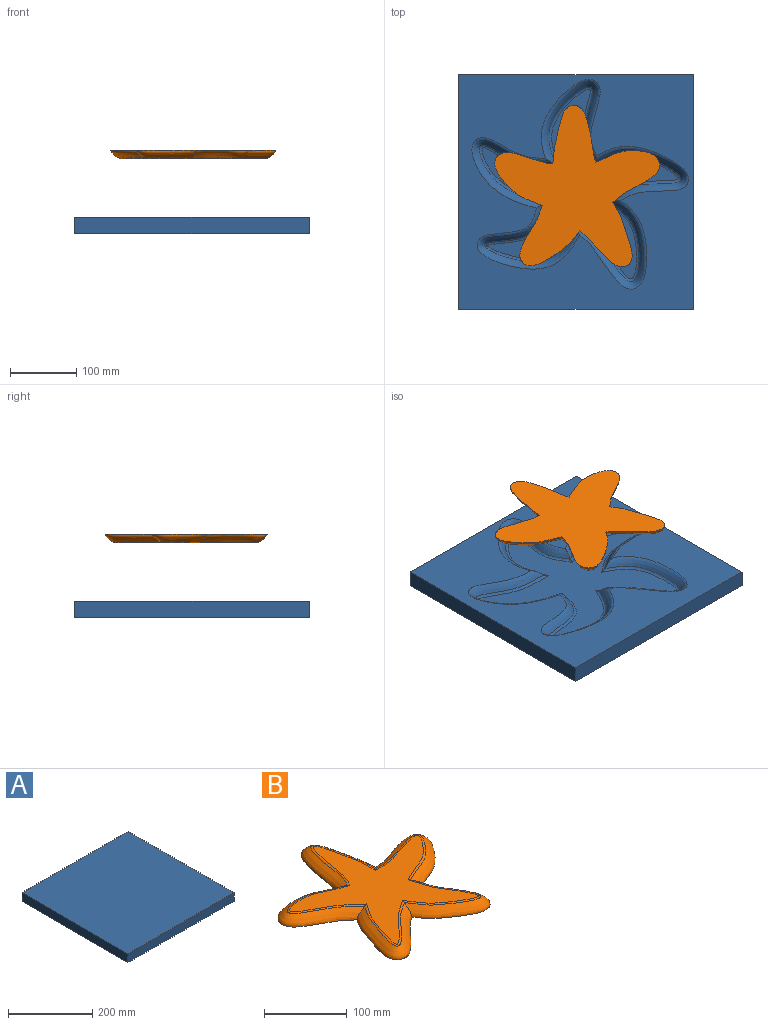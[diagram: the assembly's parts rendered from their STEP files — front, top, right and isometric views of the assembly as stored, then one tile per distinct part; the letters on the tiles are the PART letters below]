
ASSEMBLY  parts=2 mates=1
PART A: 19 faces, bbox 355.6x355.6x25.4 mm
  f0: plane 355.6x355.6mm, normal (0,0,-1), area 78097.3mm2, adj f1,f2,f3,f4,f7,f8,f9,f10
  f1: plane 355.6x25.4mm, normal (1,0,0), area 9032.2mm2, adj f0,f2,f4,f5
  f2: plane 355.6x25.4mm, normal (0,1,0), area 9032.2mm2, adj f0,f1,f3,f5
  f3: plane 355.6x25.4mm, normal (-1,0,0), area 9032.2mm2, adj f0,f2,f4,f5
  f4: plane 355.6x25.4mm, normal (0,-1,0), area 9032.2mm2, adj f0,f1,f3,f5
  f5: plane 355.6x355.6mm, normal (0,0,1), area 126451.4mm2, adj f1,f2,f3,f4
  f6: plane 297.23x287.11mm, normal (0,0,-1), area 27777.5mm2, adj f13,f14,f15,f16,f17,f18
  f7: bspline ~142.68x85.34mm, area 4168mm2, adj f0,f8,f11,f15,f17
  f8: bspline ~133.93x108.95mm, area 4339.6mm2, adj f0,f7,f9,f13,f15
  f9: bspline ~154.2x101.43mm, area 4797.9mm2, adj f0,f8,f10,f12,f13,f14,f16
  f10: bspline ~132.62x106.84mm, area 4198.7mm2, adj f0,f9,f11,f16,f18
  f11: bspline ~134.44x89.26mm, area 4397.8mm2, adj f0,f7,f10,f17,f18
  f12: bspline ~5.72x4.01mm, area 10.6mm2, adj f9,f13,f14
  f13: bspline ~158.36x99.87mm, area 811.7mm2, adj f6,f8,f9,f12,f15
  f14: bspline ~96.17x73.99mm, area 612.9mm2, adj f6,f9,f12,f16
  f15: bspline ~130.39x102.72mm, area 1333.7mm2, adj f6,f7,f8,f13,f17
  f16: bspline ~122.52x86.43mm, area 1333.3mm2, adj f6,f9,f10,f14,f18
  f17: bspline ~140.51x80mm, area 1301.7mm2, adj f6,f7,f11,f15,f18
  f18: bspline ~127.18x72.33mm, area 1354.3mm2, adj f6,f10,f11,f16,f17
PART B: 12 faces, bbox 250.4x271.5x13.4 mm
  f0: plane 250.41x245.49mm, normal (0,0,-1), area 29201.4mm2, adj f2,f3,f4,f5,f6
  f1: plane 221.21x216.23mm, normal (0,0,1), area 15140.9mm2, adj f7,f8,f9,f10,f11
  f2: bspline ~101.8x79.27mm, area 3400.4mm2, adj f0,f3,f6,f10
  f3: bspline ~101.67x83.79mm, area 3323.7mm2, adj f0,f2,f4,f8,f10
  f4: bspline ~96.98x89.64mm, area 3370.3mm2, adj f0,f3,f5,f7,f8
  f5: bspline ~103.81x81.55mm, area 3349.2mm2, adj f0,f4,f6,f7,f9,f11
  f6: bspline ~103.52x65.77mm, area 3306.3mm2, adj f0,f2,f5,f10,f11
  f7: bspline ~257.84x91.64mm, area 543mm2, adj f1,f4,f5,f8,f9
  f8: bspline ~89.07x74.24mm, area 538.9mm2, adj f1,f3,f4,f7,f10
  f9: bspline ~95.73x64.68mm, area 554.3mm2, adj f1,f5,f7,f11
  f10: bspline ~116.59x69.92mm, area 558mm2, adj f1,f2,f3,f6,f8,f11
  f11: bspline ~95.51x51.9mm, area 538.1mm2, adj f1,f5,f6,f9,f10
PLACE A rot(axis=(0,-1,0),180deg) t=(-113.9,-43.1,-16.07)mm
PLACE B rot(axis=(0,-1,0),180deg) t=(-112.67,-45.41,85.34)mm
MATE slider A.f6 <-> B.f0  axis (0,0,1) through (-113.37,-43.93,-16.07)mm
